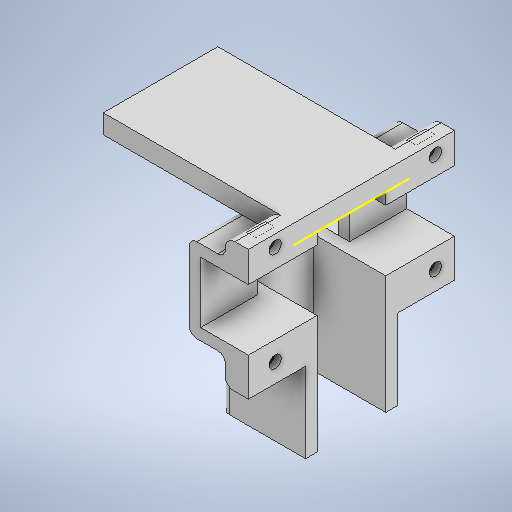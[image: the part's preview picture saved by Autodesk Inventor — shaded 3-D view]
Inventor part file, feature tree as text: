
AUTODESK INVENTOR PART (.ipt)
format: ipt  version: 2025.1 (Build 291241020, 241B)  size: 494,080 bytes
history: native  units: in
note: dims shown in document units (in); Inventor stores cm internally (conversion verified against a paired STEP export)
features: other x5, extrude x4, sketch x4, fillet x1
ambient origin geometry x8: Origin, YZ Plane, XZ Plane, XY Plane, X Axis, Y Axis, Z Axis, Center Point
bodies: Solid1 (feature_tree)
feature tree (14):
  other  "Model1Assembly.iam"
  other  "nanoMount.ipt:1"
  other  "motorMount.ipt:1"
  other  "motorMount.ipt:2"
  other  "batteryMount.ipt:1"
  extrude  "Extrusion1"  Depth=0.0787in
  extrude  "Extrusion2"  Depth=0.3937in TaperAngle=0.0deg
  extrude  "Extrusion3"  Depth=0.3937in TaperAngle=0.0deg
  extrude  "Extrusion4"  Depth=0.3937in TaperAngle=0.0deg
  fillet  "Fillet1"  Radius=0.0787in
  sketch  "Sketch4"  dims[d0=0.3937in d1=0.0787in]
  sketch  "Sketch5"  dims[d2=0.3937in d3=0.0in d4=0.3937in d5=0.0in]
  sketch  "Sketch6"  dims[d6=0.6299in d7=0.3937in d8=0.0in]
  sketch  "Sketch8"  dims[d9=0.315in d10=0.3937in d11=0.0in d12=0.0787in d13=0.0in d14=0.0in d15=0.0in]
